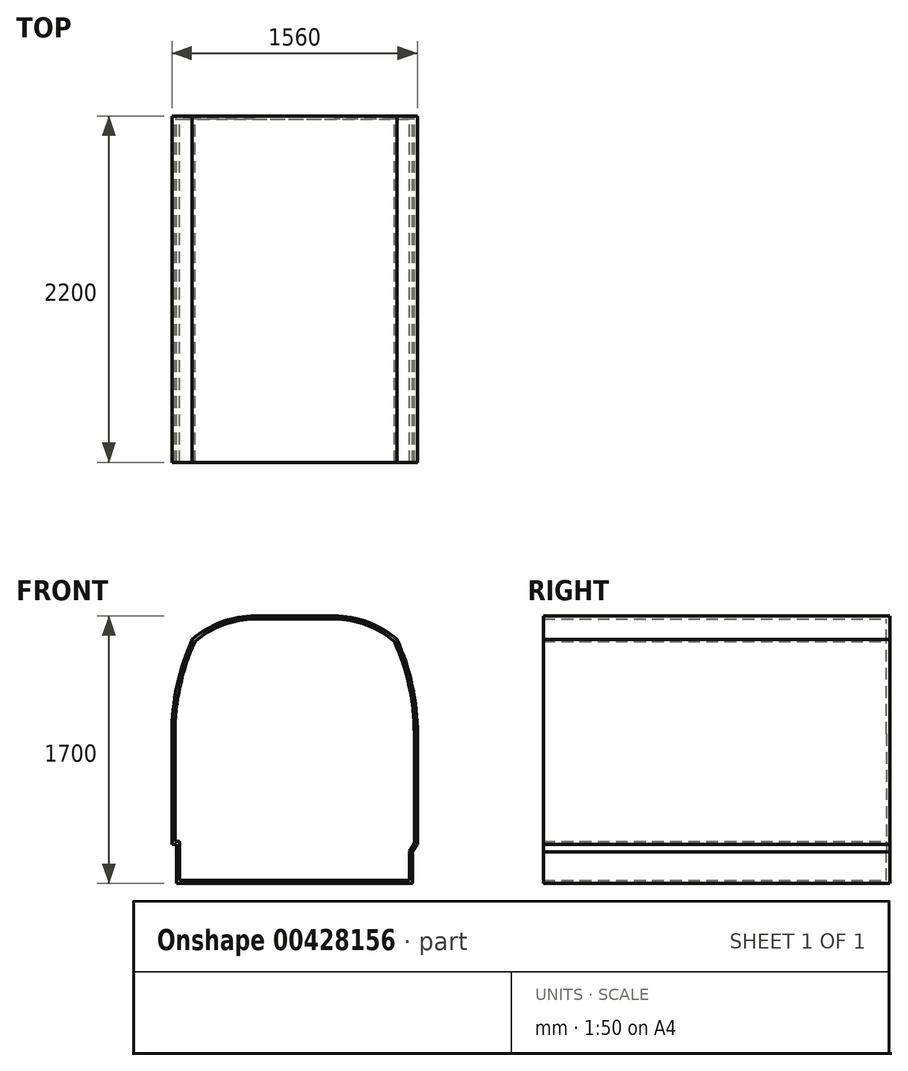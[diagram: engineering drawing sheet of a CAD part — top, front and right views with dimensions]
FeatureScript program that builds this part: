
annotation { "Feature Type Name" : "Feature", "Feature Type Description" : "" }
export const myFeature = defineFeature(function(context is Context, id is Id, definition is map)
    precondition{}
    {
        {
            var Q0;
            Q0=qCreatedBy(makeId("Front.planeOp"),FACE);
            var sketch = newSketch(context, id + "F0", { "sketchPlane" : qUnion([Q0])});
            skLineSegment(sketch, "E0", {"start": v(-750, 0) * mm, "end": v(750, 0) * mm});
            skLineSegment(sketch, "E1", {"start": v(-750, 0) * mm, "end": v(-750, 400) * mm});
            skLineSegment(sketch, "E2", {"start": v(750, 0) * mm, "end": v(750, 400) * mm});
            skLineSegment(sketch, "E3", {"start": v(-750, 400) * mm, "end": v(750, 400) * mm, "construction": true});
            skLineSegment(sketch, "E4", {"start": v(-250, 1700) * mm, "end": v(250, 1700) * mm});
            skLineSegment(sketch, "E5", {"start": v(0, 0) * mm, "end": v(0, 1700) * mm, "construction": true});
            skLineSegment(sketch, "E6", {"start": v(-650, 1550) * mm, "end": v(650, 1550) * mm, "construction": true});
            skPoint(sketch, "E7", {"position": v(0, 1550) * mm});
            skArc(sketch, "E8", {"start": v(-250, 1700) * mm, "mid": v(-463.6, 1661.27) * mm, "end": v(-650, 1550) * mm});
            skArc(sketch, "E9", {"start": v(250, 1700) * mm, "mid": v(463.6, 1661.27) * mm, "end": v(650, 1550) * mm});
            skArc(sketch, "E10", {"start": v(-780, 950) * mm, "mid": v(-747.13, 1256.96) * mm, "end": v(-650, 1550) * mm});
            skPoint(sketch, "E11", {"position": v(-691.04, 1450) * mm});
            skCircle(sketch, "E12", {"center": v(-691.04, 1450) * mm, "radius": 1203.3 * mm, "construction": true});
            skLineSegment(sketch, "E13", {"start": v(-1650, 400) * mm, "end": v(-450, 400) * mm, "construction": true});
            skLineSegment(sketch, "E14", {"start": v(-1650, 400) * mm, "end": v(-1650, 723.15) * mm, "construction": true});
            skLineSegment(sketch, "E15", {"start": v(-780, 950) * mm, "end": v(-780, 250) * mm});
            skArc(sketch, "E16.MirrorCS", {"start": v(780, 950) * mm, "mid": v(747.13, 1256.96) * mm, "end": v(650, 1550) * mm});
            skLineSegment(sketch, "E17.MirrorCS", {"start": v(780, 950) * mm, "end": v(780, 250) * mm});
            skLineSegment(sketch, "E18", {"start": v(780, 250) * mm, "end": v(750, 200) * mm});
            skLineSegment(sketch, "E19", {"start": v(-780, 250) * mm, "end": v(-750, 247.78) * mm});
            skSolve(sketch);
        }
        {
            var Q0;
            Q0 = qSketchRegion(id + "F0", true);
            extrude(context, id + "F1", {"entities" : qUnion([Q0]), "depth" : 2200 * mm});
        }
        {
            var Q0;
            Q0=makeQuery(id+"F1.opExtrude","CAP_FACE",FACE,{"disambiguationData":[OSD([sQuery(id+"F0.wireOp",EDGE,"E0"),sQuery(id+"F0.wireOp",EDGE,"E1"),sQuery(id+"F0.wireOp",EDGE,"E2"),sQuery(id+"F0.wireOp",EDGE,"E4"),sQuery(id+"F0.wireOp",EDGE,"E8"),sQuery(id+"F0.wireOp",EDGE,"E9"),sQuery(id+"F0.wireOp",EDGE,"E10"),sQuery(id+"F0.wireOp",EDGE,"E15"),sQuery(id+"F0.wireOp",EDGE,"E16.MirrorCS"),sQuery(id+"F0.wireOp",EDGE,"E17.MirrorCS"),sQuery(id+"F0.wireOp",EDGE,"E18"),sQuery(id+"F0.wireOp",EDGE,"E19")])],"isStart":false});
            shell(context, id + "F2", {"entities" : qUnion([Q0]), "thickness" : 20 * mm});
        }
    });
